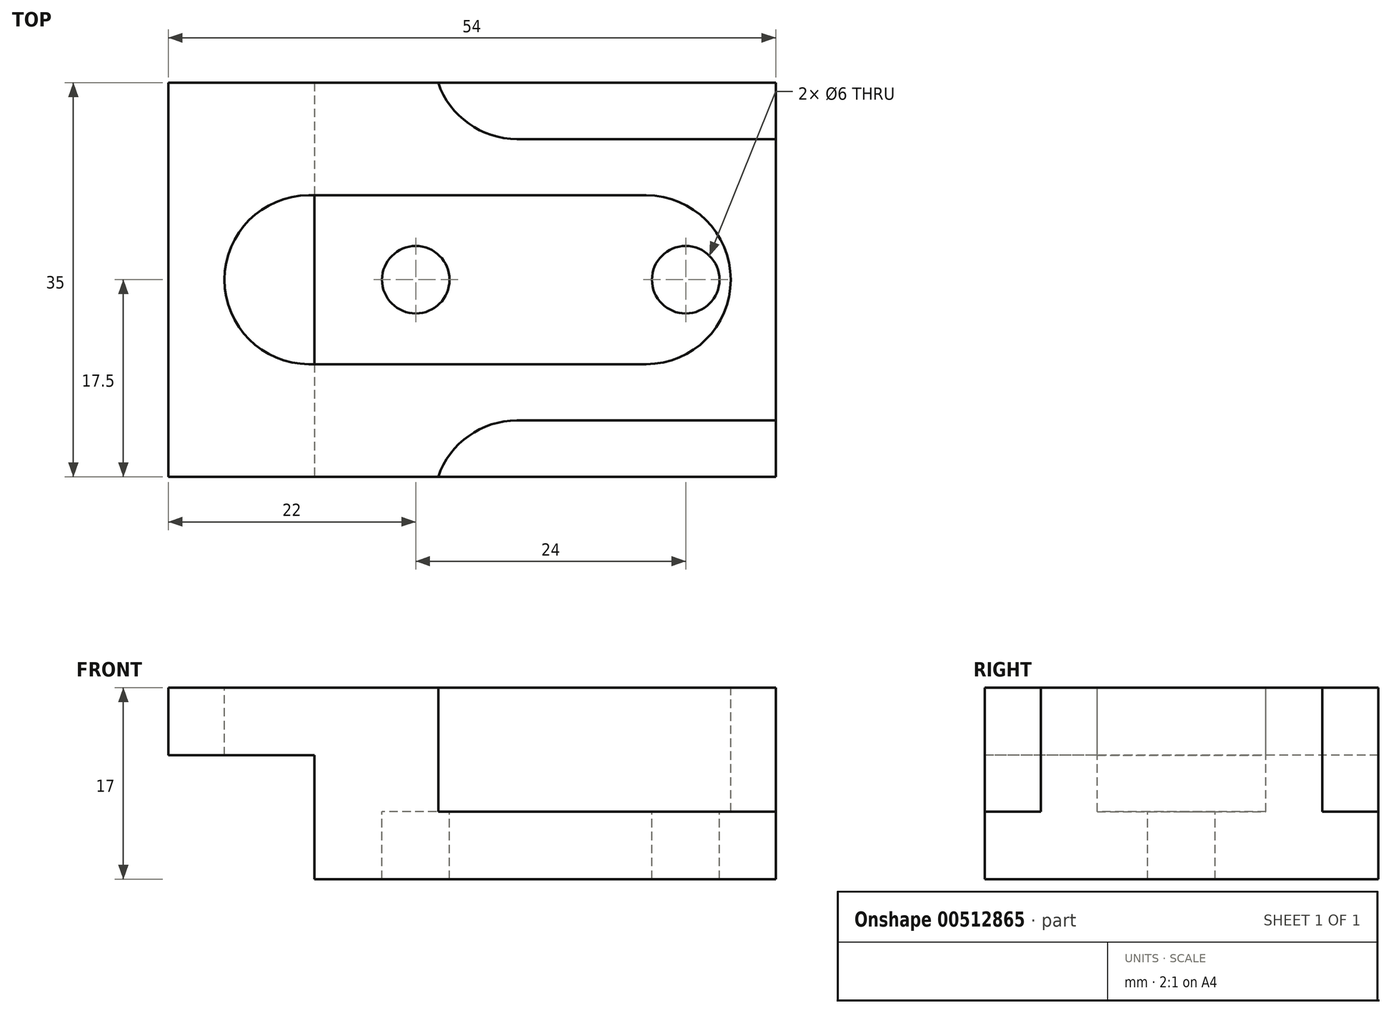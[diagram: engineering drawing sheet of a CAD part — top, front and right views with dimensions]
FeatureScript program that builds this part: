
annotation { "Feature Type Name" : "Feature", "Feature Type Description" : "" }
export const myFeature = defineFeature(function(context is Context, id is Id, definition is map)
    precondition{}
    {
        {
            var Q0;
            Q0=qCreatedBy(makeId("Top.planeOp"),FACE);
            var sketch = newSketch(context, id + "F0", { "sketchPlane" : qUnion([Q0])});
            skLineSegment(sketch, "E0.bottom", {"start": v(27, -17.5) * mm, "end": v(-27, -17.5) * mm});
            skLineSegment(sketch, "E0.top", {"start": v(27, 17.5) * mm, "end": v(-27, 17.5) * mm});
            skLineSegment(sketch, "E0.left", {"start": v(27, -17.5) * mm, "end": v(27, 17.5) * mm});
            skLineSegment(sketch, "E0.right", {"start": v(-27, -17.5) * mm, "end": v(-27, 17.5) * mm});
            skPoint(sketch, "E0.middle", {"position": v(0, 0) * mm});
            skSolve(sketch);
        }
        {
            var Q0;
            Q0 = qSketchRegion(id + "F0", true);
            extrude(context, id + "F1", {"entities" : qUnion([Q0]), "depth" : 17 * mm});
        }
        {
            var Q0;
            Q0=makeQuery(id+"F1.opExtrude","SWEPT_FACE",FACE,{"disambiguationData":[OSD([sQuery(id+"F0.wireOp",EDGE,"E0.bottom")])]});
            var sketch = newSketch(context, id + "F2", { "sketchPlane" : qUnion([Q0])});
            skLineSegment(sketch, "E1.bottom", {"start": v(-27, 0) * mm, "end": v(-14, 0) * mm});
            skLineSegment(sketch, "E1.top", {"start": v(-27, 11) * mm, "end": v(-14, 11) * mm});
            skLineSegment(sketch, "E1.left", {"start": v(-27, 0) * mm, "end": v(-27, 11) * mm});
            skLineSegment(sketch, "E1.right", {"start": v(-14, 0) * mm, "end": v(-14, 11) * mm});
            skSolve(sketch);
        }
        {
            var Q0;
            Q0 = qSketchRegion(id + "F2", true);
            extrude(context, id + "F3", {"entities" : qUnion([Q0]), "operationType" : NewBodyOperationType.REMOVE, "oppositeDirection" : true, "depth" : 35 * mm});
        }
        {
            var Q0;
            Q0=makeQuery(id+"F1.opExtrude","CAP_FACE",FACE,{"disambiguationData":[OSD([sQuery(id+"F0.wireOp",EDGE,"E0.bottom"),sQuery(id+"F0.wireOp",EDGE,"E0.top"),sQuery(id+"F0.wireOp",EDGE,"E0.left"),sQuery(id+"F0.wireOp",EDGE,"E0.right")])],"isStart":false});
            var sketch = newSketch(context, id + "F4", { "sketchPlane" : qUnion([Q0])});
            skLineSegment(sketch, "E2.bottom", {"start": v(27, -17.5) * mm, "end": v(4, -17.5) * mm});
            skLineSegment(sketch, "E2.top", {"start": v(27, -12.5) * mm, "end": v(4, -12.5) * mm});
            skLineSegment(sketch, "E2.left", {"start": v(27, -17.5) * mm, "end": v(27, -12.5) * mm});
            skLineSegment(sketch, "E3", {"start": v(4, -17.5) * mm, "end": v(-3, -17.5) * mm});
            skArc(sketch, "E4", {"start": v(4, -12.5) * mm, "mid": v(-0.3, -13.88) * mm, "end": v(-3, -17.5) * mm});
            skLineSegment(sketch, "E5", {"start": v(0, 0) * mm, "end": v(12.72, 0) * mm, "construction": true});
            skArc(sketch, "E6.MirrorCS", {"start": v(4, 12.5) * mm, "mid": v(-0.3, 13.88) * mm, "end": v(-3, 17.5) * mm});
            skLineSegment(sketch, "E7.MirrorCS", {"start": v(4, 17.5) * mm, "end": v(-3, 17.5) * mm});
            skLineSegment(sketch, "E8.MirrorCS", {"start": v(27, 17.5) * mm, "end": v(4, 17.5) * mm});
            skLineSegment(sketch, "E9.MirrorCS", {"start": v(27, 12.5) * mm, "end": v(4, 12.5) * mm});
            skLineSegment(sketch, "E10.MirrorCS", {"start": v(27, 17.5) * mm, "end": v(27, 12.5) * mm});
            skSolve(sketch);
        }
        {
            var Q0;
            Q0 = qSketchRegion(id + "F4", true);
            extrude(context, id + "F5", {"entities" : qUnion([Q0]), "operationType" : NewBodyOperationType.REMOVE, "oppositeDirection" : true, "depth" : 11 * mm});
        }
        {
            var Q0;
            Q0=makeQuery(id+"F1.opExtrude","CAP_FACE",FACE,{"disambiguationData":[OSD([sQuery(id+"F0.wireOp",EDGE,"E0.bottom"),sQuery(id+"F0.wireOp",EDGE,"E0.top"),sQuery(id+"F0.wireOp",EDGE,"E0.left"),sQuery(id+"F0.wireOp",EDGE,"E0.right")])],"isStart":false});
            var sketch = newSketch(context, id + "F6", { "sketchPlane" : qUnion([Q0])});
            skLineSegment(sketch, "E11.bottom", {"start": v(15.5, -7.5) * mm, "end": v(-14.5, -7.5) * mm});
            skLineSegment(sketch, "E11.top", {"start": v(15.5, 7.5) * mm, "end": v(-14.5, 7.5) * mm});
            skLineSegment(sketch, "E11.left", {"start": v(15.5, -7.5) * mm, "end": v(15.5, 7.5) * mm});
            skLineSegment(sketch, "E11.right", {"start": v(-14.5, -7.5) * mm, "end": v(-14.5, 7.5) * mm});
            skArc(sketch, "E12", {"start": v(-14.5, 7.5) * mm, "mid": v(-22, 0) * mm, "end": v(-14.5, -7.5) * mm});
            skArc(sketch, "E13", {"start": v(15.5, -7.5) * mm, "mid": v(23, 0) * mm, "end": v(15.5, 7.5) * mm});
            skCircle(sketch, "E14", {"center": v(19, 0) * mm, "radius": 3 * mm});
            skCircle(sketch, "E15", {"center": v(-5, 0) * mm, "radius": 3 * mm});
            skSolve(sketch);
        }
        {
            var Q0;
            Q0 = qSketchRegion(id + "F6", true);
            extrude(context, id + "F7", {"entities" : qUnion([Q0]), "operationType" : NewBodyOperationType.REMOVE, "oppositeDirection" : true, "depth" : 11 * mm});
        }
        {
            var Q0;
            Q0=makeQuery(id+"F7.boolean.opBoolean","SPLIT",FACE,{"disambiguationData":[TD([makeQuery(id+"F7.opExtrude","SWEPT_FACE",FACE,{"disambiguationData":[OSD([sQuery(id+"F6.wireOp",EDGE,"E15")])]})])],"derivedFrom":makeQuery(id+"F1.opExtrude","CAP_FACE",FACE,{"disambiguationData":[OSD([sQuery(id+"F0.wireOp",EDGE,"E0.bottom"),sQuery(id+"F0.wireOp",EDGE,"E0.top"),sQuery(id+"F0.wireOp",EDGE,"E0.left"),sQuery(id+"F0.wireOp",EDGE,"E0.right")])],"isStart":false})});
            var Q1;
            Q1=makeQuery(id+"F7.boolean.opBoolean","SPLIT",FACE,{"disambiguationData":[TD([makeQuery(id+"F7.opExtrude","SWEPT_FACE",FACE,{"disambiguationData":[OSD([sQuery(id+"F6.wireOp",EDGE,"E14")])]})])],"derivedFrom":makeQuery(id+"F1.opExtrude","CAP_FACE",FACE,{"disambiguationData":[OSD([sQuery(id+"F0.wireOp",EDGE,"E0.bottom"),sQuery(id+"F0.wireOp",EDGE,"E0.top"),sQuery(id+"F0.wireOp",EDGE,"E0.left"),sQuery(id+"F0.wireOp",EDGE,"E0.right")])],"isStart":false})});
            extrude(context, id + "F8", {"entities" : qUnion([Q0, Q1]), "operationType" : NewBodyOperationType.REMOVE, "oppositeDirection" : true, "depth" : 25 * mm});
        }
    });
